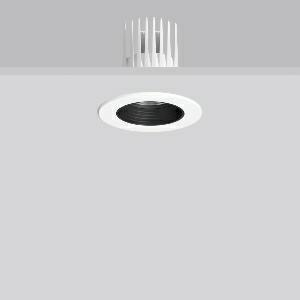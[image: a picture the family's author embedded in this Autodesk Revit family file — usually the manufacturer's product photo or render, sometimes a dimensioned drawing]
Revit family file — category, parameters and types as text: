
# Revit family: heledon_mini_e_901743_002_1_76_8ae0
name_source: partatom
category: Lighting Fixtures
units: mm (PartAtom-declared; Revit-internal decimal feet)

## family parameters
Cut with Voids When Loaded = No
Host = Face
Light Source = No
Part Type = Normal
Room Calculation Point = No
Round Connector Dimension = Use Diameter
Shared = No

## types (1)
- HELEDON mini E (1 x LED Modul 940, 2400 lm, 4000)
    Apparent Load = 20 VA
    Approval mark = CE
    CIE Flux Codes = 99 100 100 100 100
    Color Rendering = 92
    Color Temperature = 4000
    Default Elevation = 1800 mm
    Description = Series: HELEDON mini
Round recessed downlight. Housing: die-cast aluminium, powder-coated. Black plastic ring and recessed LED to prevent glare from the side. Optical assembly with lens made of plastic (polycarbonate) for the best homogeneous light distribution - can be changed without tools. Best colour rendering index Ra>90. Suitable for Recessed ceiling mounting. Installation without tools thanks to spring fastening system. Including separate LED converter with connecting cable 600 mm.High quality converter without flickering and stroboscopic effect. Through-wiring box (5 pole) available as accessory. The following accessories can be mounted without use of tools: interchangeable lenses, decorative glasses, honeycomb louvre, clear and frosted diffusers, white interchangeable plastic ring. 
Colour: traffic white, matt (RAL 9016)
Diameter: 124 mm
Height: 3 mm
Cut-out diameter: 114 mm
Recess height: 170 mm
Luminaire: recess height: 120 mm
Lamp: LED
Socket: without socket
Colour temperature: 4000K
Colour rendering index (CRI): 92
System power: 20 W
Rated luminous flux: 2400 lm
Luminous efficiency: 120 lm/W
Control gear: Converter, dimmable, DALI
Protection class: II
Type of protection: IP 20
    Height = 0 mm  [stored 0 ft]
    Lamp = 1 x LED Modul 940
    Lamp Light Flux = 2400 lm
    Lamp count = 1
    Length = 124 mm  [stored 0.406824 ft]
    Lifetime = 50000 h
    Luminous efficacy = 120 lm/W
    Manufacturer = RZB
    ModVariant = No
    Model = 901743.002.1.76
    Mounting Place = Ceiling
    Mounting Type = Recessed
    Number of Poles = 1
    OnlyDefault = Yes
    Power Factor = 1
    Product Name = HELEDON mini E
    Product group = Recessed downlights
    ProductGroupID = 402
    Protection Class = Protection class II
    Protection Degree = IP 20
    RLX_Detail_Level = 1
    RLX_Emergency_Light_Flux = 0 lm
    RLX_Emergency_Type = 0
    RLX_Emergency_Type_DB = No
    RlxData = <blob elided: 126757 chars, md5=27f3be5f>
    Socket = socket
    Standby Power = 0 W
    System Light Flux = 2400 lm
    System Power = 20 W
    Type Comments = Product without accessories
    Type Image = 901656.002.jpg
    URL = http://relux.com
    VarID = ---
    Voltage = 230 V
    Voltage Range = 220-240 V
    Weight = 0.00 kg
    Width = 0 mm  [stored 0 ft]

note: [stored X ft] marks values corroborated as IEEE doubles in the binary element streams (Revit-internal decimal feet)

## geometry (parser evidence)
native form markers: Blend x4, Sweep x11
no freeform markers — native parametric forms only
